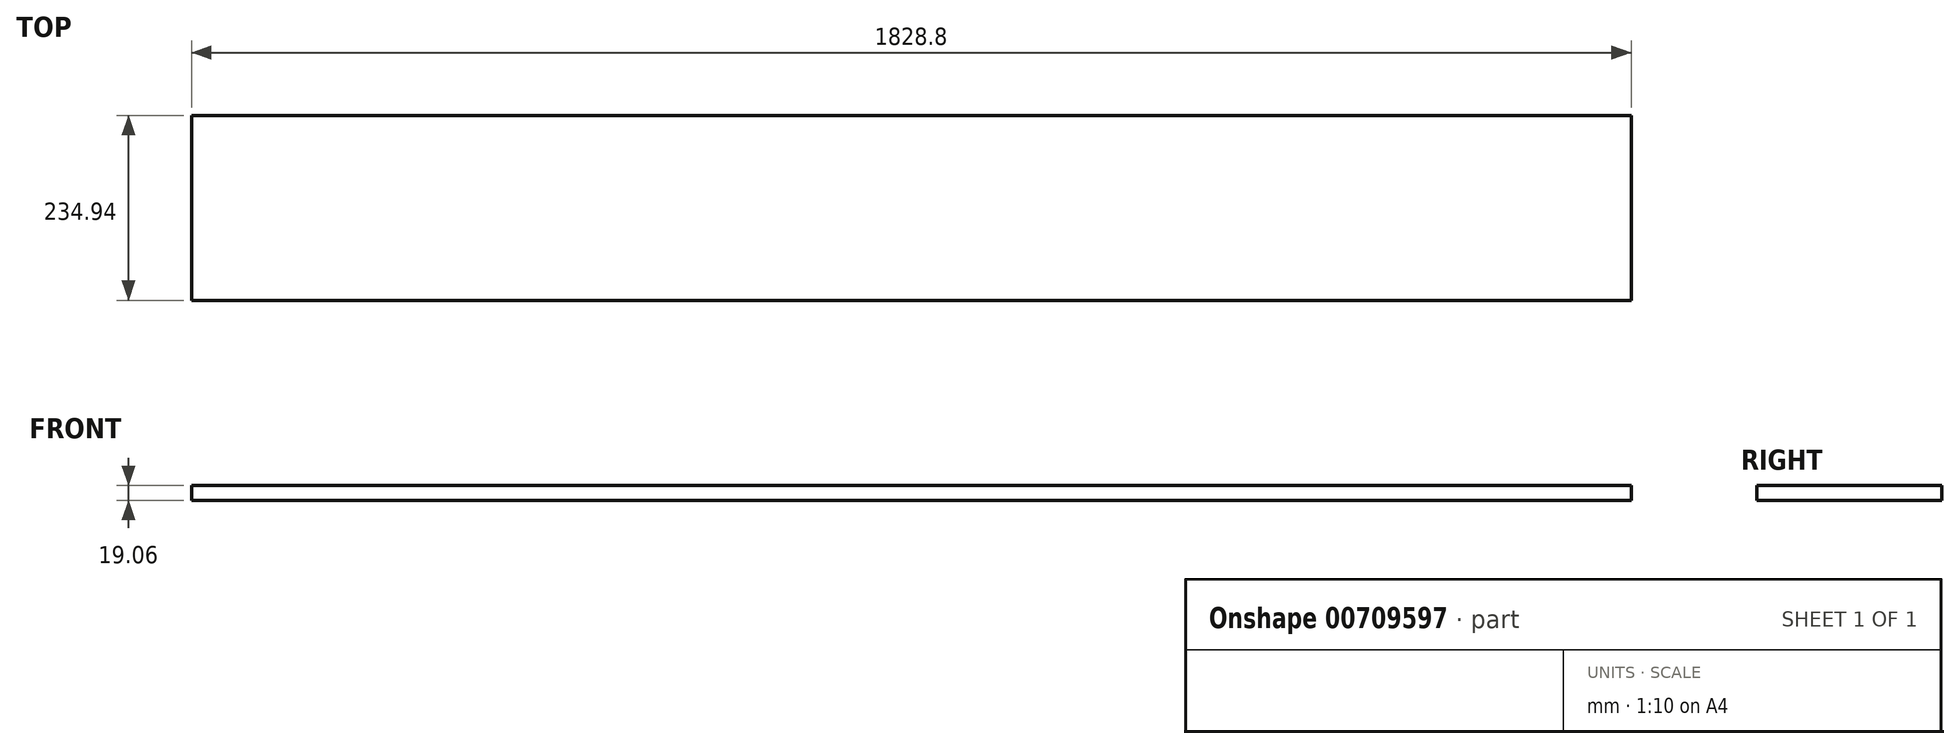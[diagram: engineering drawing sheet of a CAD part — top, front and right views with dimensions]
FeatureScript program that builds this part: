
annotation { "Feature Type Name" : "Feature", "Feature Type Description" : "" }
export const myFeature = defineFeature(function(context is Context, id is Id, definition is map)
    precondition{}
    {
        {
            var Q0;
            Q0=qCreatedBy(makeId("Top.planeOp"),FACE);
            var sketch = newSketch(context, id + "F0", { "sketchPlane" : qUnion([Q0])});
            skLineSegment(sketch, "E0.bottom", {"start": v(914.4, -117.47) * mm, "end": v(-914.4, -117.47) * mm});
            skLineSegment(sketch, "E0.top", {"start": v(914.4, 117.48) * mm, "end": v(-914.4, 117.47) * mm});
            skLineSegment(sketch, "E0.left", {"start": v(914.4, -117.47) * mm, "end": v(914.4, 117.48) * mm});
            skLineSegment(sketch, "E0.right", {"start": v(-914.4, -117.47) * mm, "end": v(-914.4, 117.48) * mm});
            skPoint(sketch, "E0.middle", {"position": v(0, 0) * mm});
            skSolve(sketch);
        }
        {
            var Q0;
            Q0=makeQuery(id+"F0.imprint","IMPRINT",FACE,{"disambiguationData":[TD([[makeQuery(id+"F0.imprint","IMPRINT",EDGE,{"derivedFrom":sQuery(id+"F0.wireOp",EDGE,"E0.bottom")}),-1.0]])]});
            extrude(context, id + "F1", {"entities" : qUnion([Q0]), "endBound" : BoundingType.SYMMETRIC, "depth" : 19.05 * mm, "offsetDistance" : 25.4 * mm});
        }
    });
